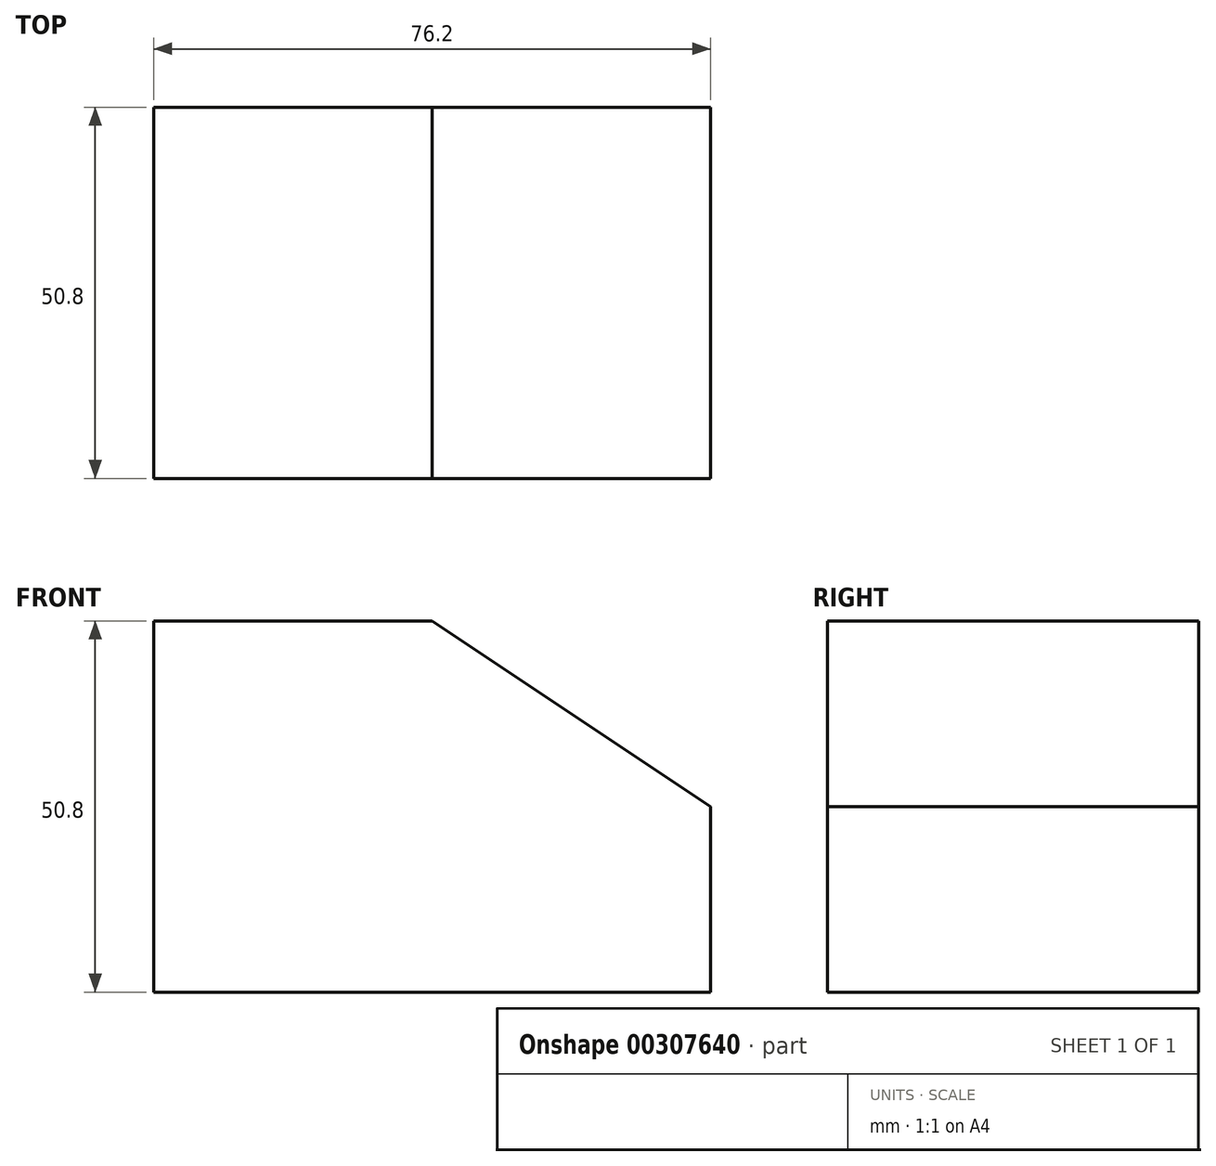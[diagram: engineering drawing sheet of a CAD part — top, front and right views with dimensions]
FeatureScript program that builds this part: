
annotation { "Feature Type Name" : "Feature", "Feature Type Description" : "" }
export const myFeature = defineFeature(function(context is Context, id is Id, definition is map)
    precondition{}
    {
        {
            var Q0;
            Q0=qCreatedBy(makeId("Front.planeOp"),FACE);
            var sketch = newSketch(context, id + "F0", { "sketchPlane" : qUnion([Q0])});
            skLineSegment(sketch, "E0", {"start": v(-44.73, -50.8) * mm, "end": v(31.47, -50.8) * mm});
            skLineSegment(sketch, "E1", {"start": v(31.47, -50.8) * mm, "end": v(31.47, -25.4) * mm});
            skLineSegment(sketch, "E2", {"start": v(-44.73, -50.8) * mm, "end": v(-44.73, 0) * mm});
            skLineSegment(sketch, "E3", {"start": v(-44.73, 0) * mm, "end": v(-6.63, 0) * mm});
            skLineSegment(sketch, "E4", {"start": v(-6.63, 0) * mm, "end": v(31.47, -25.4) * mm});
            skSolve(sketch);
        }
        {
            var Q0;
            Q0=makeQuery(id+"F0.imprint","IMPRINT",FACE,{"disambiguationData":[TD([[makeQuery(id+"F0.imprint","IMPRINT",EDGE,{"derivedFrom":sQuery(id+"F0.wireOp",EDGE,"E0")}),1.0]])]});
            extrude(context, id + "F1", {"entities" : qUnion([Q0]), "depth" : 50.8 * mm});
        }
    });
